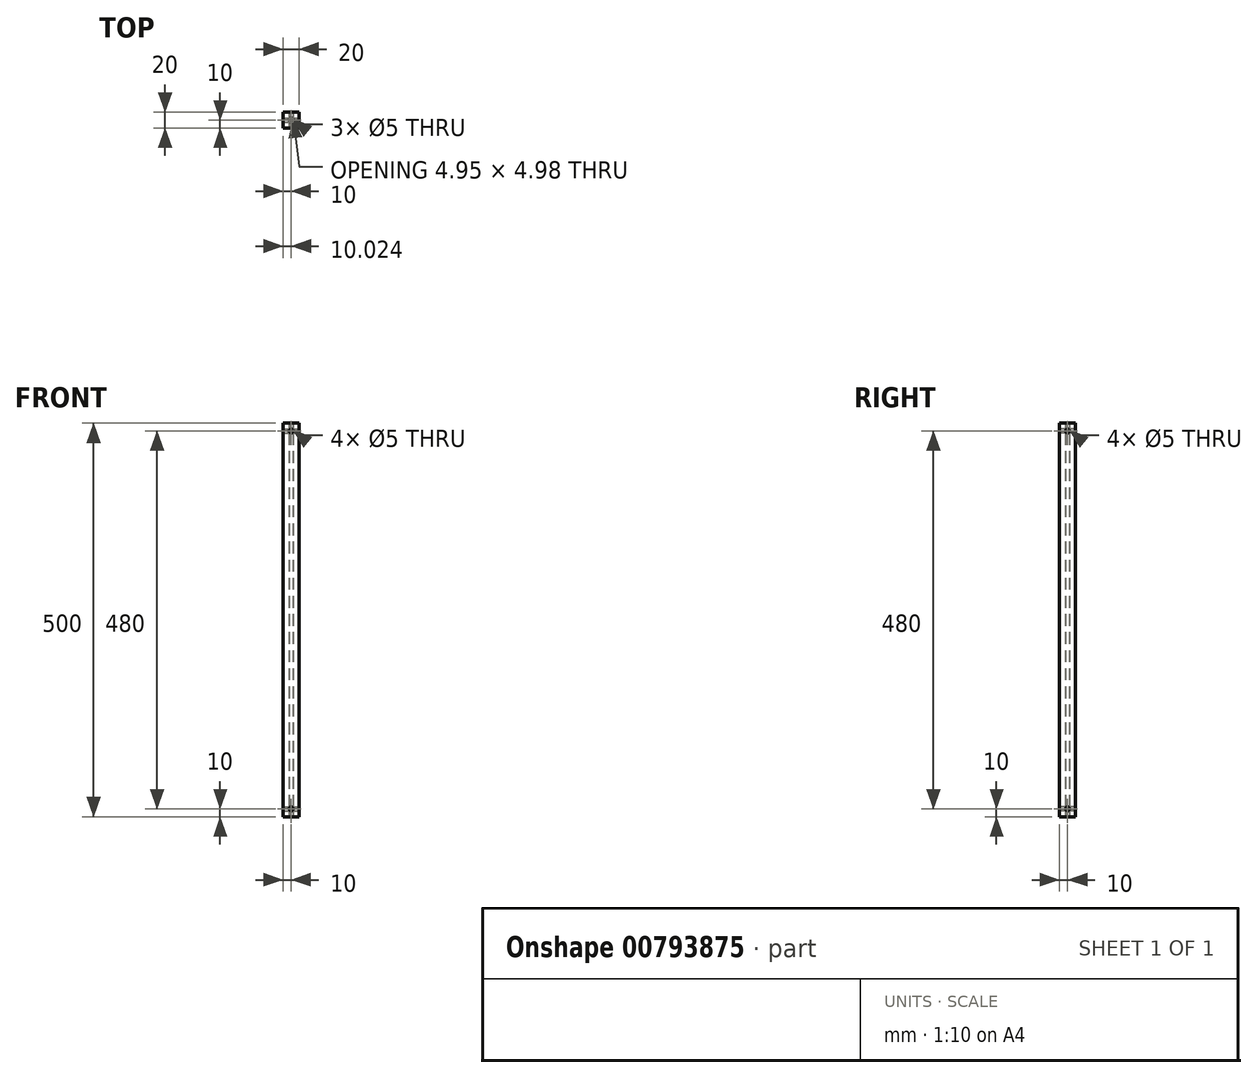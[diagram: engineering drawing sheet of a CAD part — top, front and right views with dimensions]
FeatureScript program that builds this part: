
annotation { "Feature Type Name" : "Feature", "Feature Type Description" : "" }
export const myFeature = defineFeature(function(context is Context, id is Id, definition is map)
    precondition{}
    {
        {
            var Q0;
            Q0=qCreatedBy(makeId("Top.planeOp"),FACE);
            var sketch = newSketch(context, id + "F0", { "sketchPlane" : qUnion([Q0])});
            skLineSegment(sketch, "E0.bottom", {"start": v(-10, 10) * mm, "end": v(10, 10) * mm});
            skLineSegment(sketch, "E0.top", {"start": v(-10, -10) * mm, "end": v(10, -10) * mm});
            skLineSegment(sketch, "E0.left", {"start": v(-10, 10) * mm, "end": v(-10, -10) * mm});
            skLineSegment(sketch, "E0.right", {"start": v(10, 10) * mm, "end": v(10, -10) * mm});
            skCircle(sketch, "E1", {"center": v(0, 0) * mm, "radius": 2.5 * mm});
            skSolve(sketch);
        }
        {
            var Q0;
            Q0=qSketchRegion(id+"F0",true);
            extrude(context, id + "F1", {"entities" : qUnion([Q0]), "depth" : 500 * mm});
        }
        {
            var Q0;
            Q0=makeQuery(id+"F1.opExtrude","SWEPT_FACE",FACE,{"disambiguationData":[OSD([sQuery(id+"F0.wireOp",EDGE,"E0.right")])]});
            var sketch = newSketch(context, id + "F2", { "sketchPlane" : qUnion([Q0])});
            skCircle(sketch, "E2", {"center": v(0, 10) * mm, "radius": 2.5 * mm});
            skCircle(sketch, "E3", {"center": v(0, 490) * mm, "radius": 2.5 * mm});
            skSolve(sketch);
        }
        {
            var Q0;
            Q0=qSketchRegion(id+"F2",true);
            extrude(context, id + "F3", {"entities" : qUnion([Q0]), "operationType" : NewBodyOperationType.REMOVE, "endBound" : BoundingType.THROUGH_ALL, "oppositeDirection" : true, "depth" : 25 * mm});
        }
        {
            var Q0;
            Q0=makeQuery(id+"F1.opExtrude","SWEPT_FACE",FACE,{"disambiguationData":[OSD([sQuery(id+"F0.wireOp",EDGE,"E0.top")])]});
            var sketch = newSketch(context, id + "F4", { "sketchPlane" : qUnion([Q0])});
            skCircle(sketch, "E4", {"center": v(0, 490) * mm, "radius": 2.5 * mm});
            skCircle(sketch, "E5", {"center": v(0, 10) * mm, "radius": 2.5 * mm});
            skSolve(sketch);
        }
        {
            var Q0;
            Q0=qSketchRegion(id+"F4",true);
            extrude(context, id + "F5", {"entities" : qUnion([Q0]), "operationType" : NewBodyOperationType.REMOVE, "endBound" : BoundingType.THROUGH_ALL, "oppositeDirection" : true, "depth" : 25 * mm});
        }
    });
